SOLIDWORKS PART (.sldprt)
format: sldprt  version: not decoded by parser v0  size: 135,680 bytes
history: native  units: mm
features: sketch x5, plane x4, extrude x3, shell x2, material x1, cut_extrude x1 (+13 scaffold rows collapsed)
feature tree (29):
  scaffold x13  (default folders/planes/origin — collapsed)
  material  "材质 <未指定>"
  plane  "前视基准面"
  plane  "上视基准面"
  plane  "右视基准面"
  sketch  "草图1"  dims[D1=150.0mm D2=200.0mm]
  extrude  "凸台-拉伸1"  Depth=50mm
  sketch  "草图2"
  plane  "基准面1"
  sketch  "草图3"  dims[D1=50.0mm D2=140.0mm]
  extrude  "凸台-拉伸2"  Depth=40mm
  shell  "抽壳1"  Thickness=3mm
  shell  "抽壳2"  Thickness=3mm
  sketch  "草图4"  dims[D1=10.0mm]
  extrude  "凸台-拉伸3"  Depth=280mm
  sketch  "草图5"  dims[D1=150.0mm]
  cut_extrude  "切除-拉伸1"  Depth=1500mm
decode coverage: 10 of 11 modeling features carry decoded parameters
note: suppression state not decoded; provenance and decode notes live in map.json
